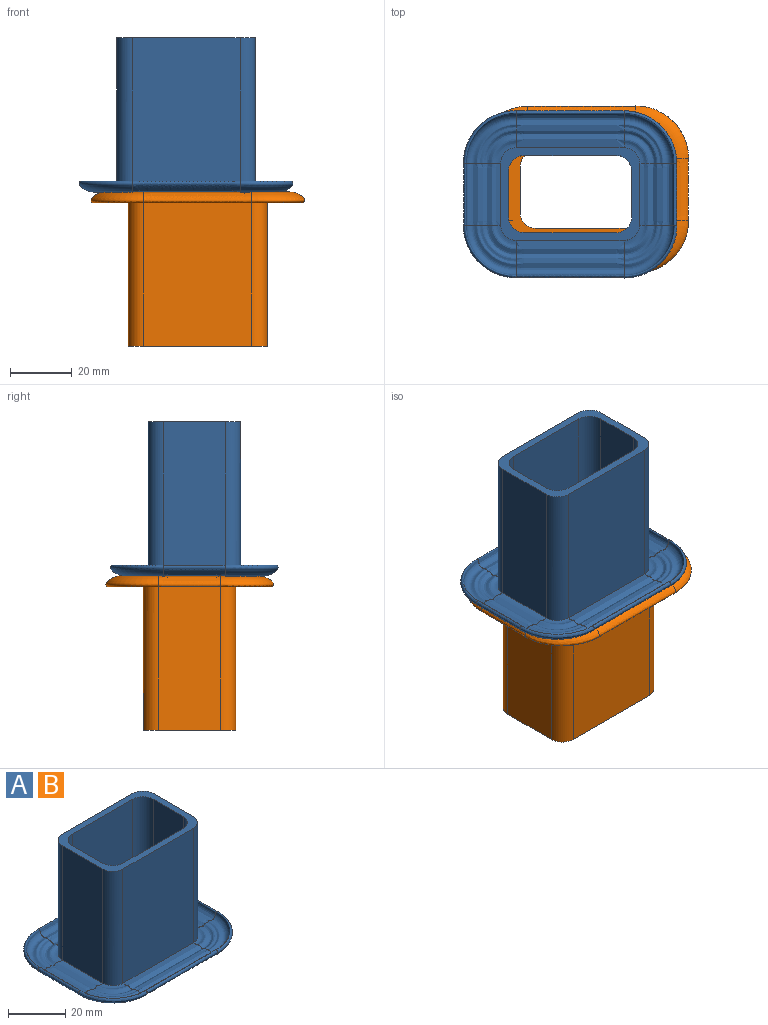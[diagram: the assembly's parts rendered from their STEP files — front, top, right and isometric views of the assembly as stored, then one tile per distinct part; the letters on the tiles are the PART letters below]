
ASSEMBLY  parts=2 mates=1
PART A: 71 faces, bbox 107.4x92.3x88 mm
  f0: plane 1.69x0.45mm, normal (0,-1,0), area 0mm2, adj f41,f70
  f1: plane 1.51x0.73mm, normal (0,-1,0), area 0mm2, adj f41,f70
  f2: plane 0.93x0.34mm, normal (0,-1,0), area 0mm2, adj f41,f70
  f3: plane 2.62x2.37mm, normal (0,-1,0), area 0.1mm2, adj f41,f70
  f4: plane 1.05x0.02mm, normal (0,-1,0), area 0mm2, adj f39,f41,f70
  f5: plane 2.54x1.91mm, normal (-1,0,0), area 0.2mm2, adj f56,f70
  f6: plane 0.57x0.27mm, normal (-1,0,0), area 0mm2, adj f56,f70
  f7: plane 1.06x0.64mm, normal (-1,0,0), area 0mm2, adj f56,f70
  f8: plane 0.69x0.27mm, normal (-1,0,0), area 0mm2, adj f56,f70
  f9: plane 3.21x0.3mm, normal (-1,0,0), area 0mm2, adj f56,f70
  f10: cylinder r=5mm len=49.11mm, axis (0,0,-1), area 385.7mm2, adj f18,f27,f38,f58
  f11: plane 1.55x0.58mm, normal (-1,0,0), area 0mm2, adj f50,f58
  f12: plane 49.1x35mm, normal (0,-1,0), area 1718.6mm2, adj f19,f28,f38,f56
  f13: plane 4.6x3.78mm, normal (-1,0,0), area 0.5mm2, adj f48,f56
  f14: plane 1.95x0.54mm, normal (-1,0,0), area 0.1mm2, adj f48,f56
  f15: plane 1.11x0.16mm, normal (-1,0,0), area 0mm2, adj f48,f56
  f16: plane 2.21x0.73mm, normal (-1,0,0), area 0.2mm2, adj f48,f56
  f17: plane 1.44x0.15mm, normal (-1,0,0), area 0mm2, adj f48,f56
  f18: plane 49.1x35mm, normal (0,1,0), area 1718.6mm2, adj f10,f37,f38,f50
  f19: cylinder r=5mm len=49.1mm, axis (0,0,-1), area 385.7mm2, adj f12,f26,f38,f48
  f20: plane 2.62x2.42mm, normal (0,-1,0), area 0.3mm2, adj f40,f48
  f21: plane 0.97x0.34mm, normal (0,-1,0), area 0mm2, adj f40,f48
  f22: plane 1.56x0.73mm, normal (0,-1,0), area 0.1mm2, adj f40,f48
  f23: plane 1.88x0.45mm, normal (0,-1,0), area 0mm2, adj f40,f48
  f24: plane 0.8x0.02mm, normal (0,-1,0), area 0mm2, adj f39,f40,f48
  f25: plane 39.33x38.55mm, normal (0,1,0), area 0mm2, adj f40,f43
  f26: plane 49.11x20mm, normal (1,0,0), area 982.1mm2, adj f19,f37,f38,f40,f47
  f27: plane 49.11x20mm, normal (-1,0,0), area 982.1mm2, adj f10,f28,f38,f41
  f28: cylinder r=5mm len=49.11mm, axis (0,0,-1), area 385.7mm2, adj f12,f27,f38,f70
  f29: cylinder r=5mm len=50mm, axis (0,0,-1), area 392.7mm2, adj f30,f36,f38,f39
  f30: plane 50x30mm, normal (0,-1,0), area 1500mm2, adj f29,f31,f38,f39
  f31: cylinder r=5mm len=50mm, axis (0,0,-1), area 392.7mm2, adj f30,f32,f38,f39
  f32: plane 50x15mm, normal (-1,0,0), area 750mm2, adj f31,f33,f38,f39
  f33: cylinder r=5mm len=50mm, axis (0,0,-1), area 392.7mm2, adj f32,f34,f38,f39
  f34: plane 50x30mm, normal (0,1,0), area 1500mm2, adj f33,f35,f38,f39
  f35: cylinder r=5mm len=50mm, axis (0,0,-1), area 392.7mm2, adj f34,f36,f38,f39
  f36: plane 50x15mm, normal (1,0,0), area 750mm2, adj f29,f35,f38,f39
  f37: cylinder r=5mm len=49.11mm, axis (0,0,-1), area 385.7mm2, adj f18,f26,f38,f43
  f38: plane 45x30mm, normal (0,0,1), area 350mm2, adj f10,f12,f18,f19,f26,f27,f28,f29
  f39: plane 56.38x41.38mm, normal (0,0,-1), area 1254mm2, adj f4,f24,f29,f30,f31,f32,f33,f34
  f40: extruded ~20x12.06mm, area 428.9mm2, adj f20,f21,f22,f23,f24,f25,f26,f39
  f41: extruded ~20x12.06mm, area 429mm2, adj f0,f1,f2,f3,f4,f27,f39,f42
  f42: plane 12.27x3.8mm, normal (0,1,0), area 12.2mm2, adj f39,f41,f59
  f43: revolved ~34.18x34.18mm, area 252.8mm2, adj f25,f37,f39,f40,f50
  f44: plane 6.01x3.8mm, normal (0,1,0), area 0.4mm2, adj f40,f48
  f45: plane 1.56x0.52mm, normal (0,1,0), area 0mm2, adj f40,f48
  f46: plane 0.75x0.11mm, normal (0,1,0), area 0mm2, adj f40,f48
  f47: plane 0.89x0.1mm, normal (0,1,0), area 0mm2, adj f26,f40,f48
  f48: revolved ~17.16x17.16mm, area 438mm2, adj f13,f14,f15,f16,f17,f19,f20,f21
  f49: plane 1.86x0.7mm, normal (0,1,0), area 0.1mm2, adj f40,f48
  f50: extruded ~35x12.1mm, area 752mm2, adj f11,f18,f39,f43,f51,f57,f60
  f51: plane 6.27x2.17mm, normal (-1,0,0), area 0.1mm2, adj f50,f58
  f52: plane 2.58x2.09mm, normal (1,0,0), area 0.4mm2, adj f48,f56
  f53: plane 0.72x0.3mm, normal (1,0,0), area 0mm2, adj f48,f56
  f54: plane 1.24x0.69mm, normal (1,0,0), area 0.1mm2, adj f48,f56
  f55: plane 1.08x0.38mm, normal (1,0,0), area 0mm2, adj f48,f56
  f56: extruded ~35x12mm, area 744.7mm2, adj f5,f6,f7,f8,f9,f12,f13,f14
  f57: plane 1.63x0.94mm, normal (1,0,0), area 0.1mm2, adj f50,f58
  f58: revolved ~17.13x17.12mm, area 436.1mm2, adj f10,f11,f39,f51,f57,f59,f60
  f59: plane 12.29x3.79mm, normal (0,-1,0), area 12.4mm2, adj f39,f42,f58
  f60: plane 10.82x1.48mm, normal (1,0,0), area 0.3mm2, adj f50,f58
  f61: plane 5.71x3.79mm, normal (0,1,0), area 0.2mm2, adj f41,f70
  f62: plane 1.61x0.52mm, normal (0,1,0), area 0mm2, adj f41,f70
  f63: plane 0.8x0.11mm, normal (0,1,0), area 0mm2, adj f41,f70
  f64: plane 1.9x0.7mm, normal (0,1,0), area 0mm2, adj f41,f70
  f65: plane 3.6x3.57mm, normal (1,0,0), area 0.3mm2, adj f56,f70
  f66: plane 2.17x0.55mm, normal (1,0,0), area 0.1mm2, adj f56,f70
  f67: plane 1.27x0.18mm, normal (1,0,0), area 0mm2, adj f56,f70
  f68: plane 2.44x0.74mm, normal (1,0,0), area 0.1mm2, adj f56,f70
  f69: plane 1.63x0.16mm, normal (1,0,0), area 0mm2, adj f56,f70
  f70: revolved ~17.1x17.1mm, area 434.5mm2, adj f0,f1,f2,f3,f4,f5,f6,f7
PART B: same geometry as A
PLACE A t=(-47.07,-6.13,100.09)mm
PLACE B rot(axis=(1,0,0),180deg) t=(-43.27,-4.63,100.09)mm
MATE planar A.f39 <-> B.f39  axis (0,0,-1) through (-47.07,-6.13,100.09)mm
